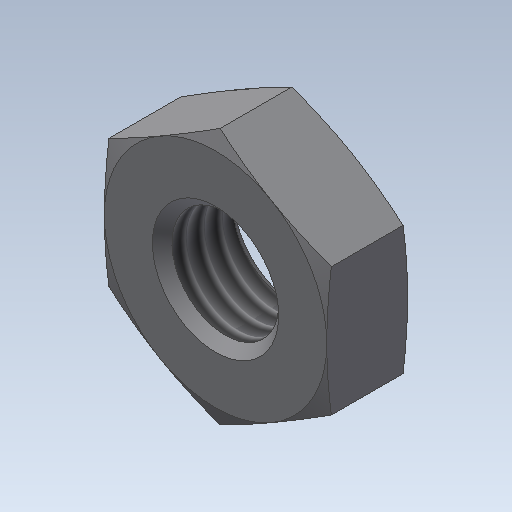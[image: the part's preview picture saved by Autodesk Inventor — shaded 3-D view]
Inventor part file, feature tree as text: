
AUTODESK INVENTOR PART (.ipt)
format: ipt  version: 2020 (Build 240168000, 168)  size: 180,224 bytes
history: native  units: in
note: dims shown in document units (in); Inventor stores cm internally (conversion verified against a paired STEP export)
features: other x70, sketch x3, revolve x2, extrude x1, thread x1
ambient origin geometry x8: Origin, YZ Plane, XZ Plane, XY Plane, X Axis, Y Axis, Z Axis, Center Point
bodies: Solid1 (feature_tree)
feature tree (77):
  sketch  "Sketch_8"  dims[d0=360.0deg d1=0.16in d2=0.0in]
  sketch  "Sketch_10"  dims[d3=360.0deg d4=0.1213in d5=0.0in]
  revolve  "Revolution1"  [1 undecoded]
  extrude  "Extrusion1"  Depth=0.1213in TaperAngle=0.0deg
  revolve  "Revolution2"  [1 undecoded]
  thread  "Thread1"  [1 undecoded]
  other  "NUT_XY"
  other  "NUT_YZ"
  other  "NUT_ZX"
  other  "NUT_X"
  other  "NUT_Y"
  other  "NUT_Z"
  other  "NUT_Center"
  other  "a1_XY"
  other  "a1_YZ"
  other  "a1_ZX"
  other  "a1_X"
  other  "a1_Y"
  other  "a1_Z"
  other  "a1_Center"
  other  "a2_XY"
  other  "a2_YZ"
  other  "a2_ZX"
  other  "a2_X"
  other  "a2_Y"
  other  "a2_Z"
  other  "a2_Center"
  other  "b1_XY"
  other  "b1_YZ"
  other  "b1_ZX"
  other  "b1_X"
  other  "b1_Y"
  other  "b1_Z"
  other  "b1_Center"
  other  "b2_XY"
  other  "b2_YZ"
  other  "b2_ZX"
  other  "b2_X"
  other  "b2_Y"
  other  "b2_Z"
  other  "b2_Center"
  other  "e_XY"
  other  "e_YZ"
  other  "e_ZX"
  other  "e_X"
  other  "e_Y"
  other  "e_Z"
  other  "e_Center"
  other  "ol1_XY"
  other  "ol1_YZ"
  other  "ol1_ZX"
  other  "ol1_X"
  other  "ol1_Y"
  other  "ol1_Z"
  other  "ol1_Center"
  other  "ol2_XY"
  other  "ol2_YZ"
  other  "ol2_ZX"
  other  "ol2_X"
  other  "ol2_Y"
  other  "ol2_Z"
  other  "ol2_Center"
  other  "th1_XY"
  other  "th1_YZ"
  other  "th1_ZX"
  other  "th1_X"
  other  "th1_Y"
  other  "th1_Z"
  other  "th1_Center"
  other  "th2_XY"
  other  "th2_YZ"
  other  "th2_ZX"
  other  "th2_X"
  other  "th2_Y"
  other  "th2_Z"
  other  "th2_Center"
  sketch  "Sketch_11"  dims[d6=0.0in d7=0.0in d8=0.0in]
note: 3 required parameter values undecoded (feature->parameter linkage not recoverable at this tier; creation-order binding heuristic only, values carry confidence <= 0.55)